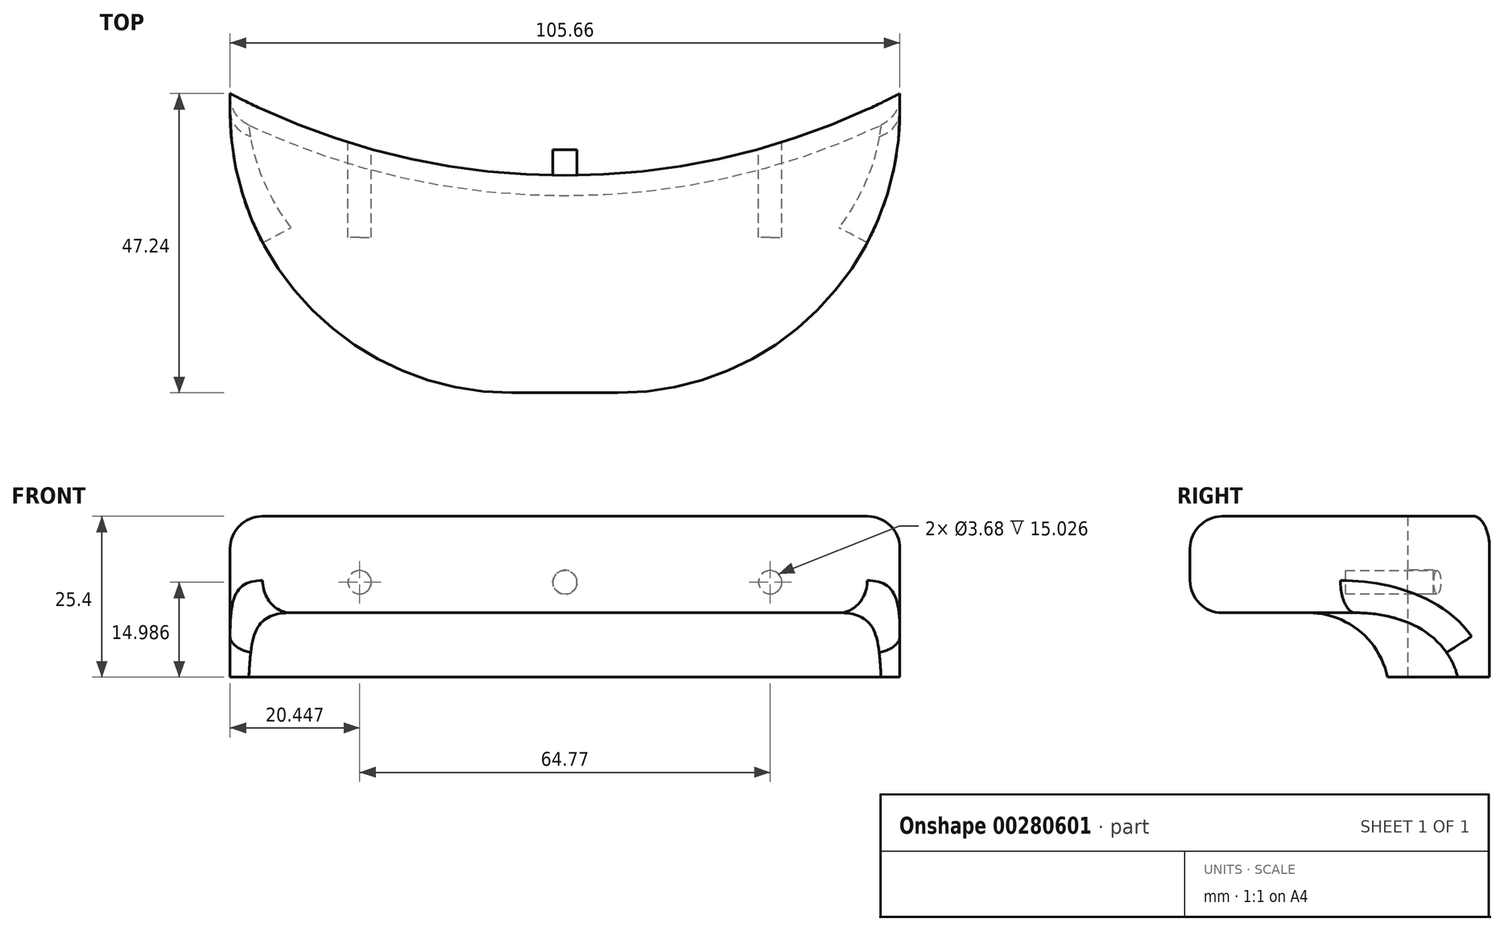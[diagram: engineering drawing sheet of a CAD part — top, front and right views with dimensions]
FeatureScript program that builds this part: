
annotation { "Feature Type Name" : "Feature", "Feature Type Description" : "" }
export const myFeature = defineFeature(function(context is Context, id is Id, definition is map)
    precondition{}
    {
        {
            var Q0;
            Q0=qCreatedBy(makeId("Top.planeOp"),FACE);
            var sketch = newSketch(context, id + "F0", { "sketchPlane" : qUnion([Q0])});
            skLineSegment(sketch, "E0.bottom", {"start": v(44.45, 0) * mm, "end": v(61.21, 0) * mm});
            skLineSegment(sketch, "E0.left", {"start": v(0, 44.45) * mm, "end": v(0, 47.24) * mm});
            skLineSegment(sketch, "E0.right", {"start": v(105.66, 44.45) * mm, "end": v(105.66, 47.24) * mm});
            skArc(sketch, "E1", {"start": v(0, 47.24) * mm, "mid": v(52.83, 34.3) * mm, "end": v(105.66, 47.24) * mm});
            skPoint(sketch, "E2.visualSharp", {"position": v(0, 0) * mm});
            skArc(sketch, "E2.filletArc", {"start": v(0, 44.45) * mm, "mid": v(13.02, 13.02) * mm, "end": v(44.45, 0) * mm});
            skPoint(sketch, "E3.visualSharp", {"position": v(105.66, 0) * mm});
            skArc(sketch, "E3.filletArc", {"start": v(61.21, 0) * mm, "mid": v(92.64, 13.02) * mm, "end": v(105.66, 44.45) * mm});
            skSolve(sketch);
        }
        {
            var Q0;
            Q0 = qSketchRegion(id + "F0", true);
            extrude(context, id + "F1", {"entities" : qUnion([Q0]), "depth" : 25.4 * mm});
        }
        {
            var Q0;
            Q0=makeQuery(id+"F1.opExtrude","CAP_FACE",FACE,{"disambiguationData":[OSD([sQuery(id+"F0.wireOp",EDGE,"E0.bottom"),sQuery(id+"F0.wireOp",EDGE,"E0.left"),sQuery(id+"F0.wireOp",EDGE,"E0.right"),sQuery(id+"F0.wireOp",EDGE,"E1"),sQuery(id+"F0.wireOp",EDGE,"E2.filletArc"),sQuery(id+"F0.wireOp",EDGE,"E3.filletArc")])],"isStart":true});
            var sketch = newSketch(context, id + "F2", { "sketchPlane" : qUnion([Q0])});
            skArc(sketch, "E4.0", {"start": v(-1.47, -44.43) * mm, "mid": v(52.83, -31.13) * mm, "end": v(107.13, -44.43) * mm});
            skLineSegment(sketch, "E5", {"start": v(-1.47, -44.43) * mm, "end": v(-1.47, 12.03) * mm});
            skLineSegment(sketch, "E6", {"start": v(107.13, -44.43) * mm, "end": v(107.13, 12.98) * mm});
            skLineSegment(sketch, "E7", {"start": v(107.13, 12.98) * mm, "end": v(-1.47, 12.03) * mm});
            skSolve(sketch);
        }
        {
            var Q0;
            Q0 = qSketchRegion(id + "F2", true);
            extrude(context, id + "F3", {"entities" : qUnion([Q0]), "operationType" : NewBodyOperationType.REMOVE, "oppositeDirection" : true, "depth" : 10.16 * mm});
        }
        {
            var Q0;
            Q0=makeQuery(id+"F3.boolean.opBoolean","COPY",EDGE,{"derivedFrom":makeQuery(id+"F3.opExtrude","CAP_EDGE",EDGE,{"disambiguationData":[OSD([sQuery(id+"F2.wireOp",EDGE,"E4.0")])],"isStart":false})});
            fillet(context, id + "F4", {"entities" : qUnion([Q0]), "radius" : 12.7 * mm, "tangentPropagation" : true, "allowEdgeOverflow" : false});
        }
        {
            var Q0;
            Q0=makeQuery(id+"F1.opExtrude","CAP_EDGE",EDGE,{"disambiguationData":[OSD([sQuery(id+"F0.wireOp",EDGE,"E2.filletArc")])],"isStart":false});
            fillet(context, id + "F5", {"entities" : qUnion([Q0]), "radius" : 5.08 * mm, "tangentPropagation" : true, "allowEdgeOverflow" : false});
        }
        {
            var Q0;
            Q0=makeQuery(id+"F3.boolean.opBoolean","INTERSECT",EDGE,{"derivedFrom":[makeQuery(id+"F1.opExtrude","SWEPT_FACE",FACE,{"disambiguationData":[OSD([sQuery(id+"F0.wireOp",EDGE,"E2.filletArc")])]}),makeQuery(id+"F3.opExtrude","CAP_FACE",FACE,{"disambiguationData":[OSD([sQuery(id+"F2.wireOp",EDGE,"E4.0"),sQuery(id+"F2.wireOp",EDGE,"E5"),sQuery(id+"F2.wireOp",EDGE,"E6"),sQuery(id+"F2.wireOp",EDGE,"E7")])],"isStart":false})]});
            fillet(context, id + "F6", {"entities" : qUnion([Q0]), "radius" : 5.08 * mm, "tangentPropagation" : true, "allowEdgeOverflow" : false});
        }
        {
            var Q0;
            Q0=makeQuery(id+"F1.opExtrude","CAP_EDGE",EDGE,{"disambiguationData":[OSD([sQuery(id+"F0.wireOp",EDGE,"E1")])],"isStart":false});
            cPoint(context, id + "F7", {"entities" : qUnion([Q0]), "parameter" : 0.5});
        }
        {
            var Q0;
            Q0=qCreatedBy(makeId("Front.planeOp"),FACE);
            var Q1;
            Q1 = qCreatedBy(id + "F7" ,VERTEX);
            cPlane(context, id + "F8", {"entities" : qUnion([Q0, Q1]), "cplaneType" : CPlaneType.PLANE_POINT, "offset" : 25.4 * mm, "oppositeDirection" : true, "width" : 152.4 * mm, "height" : 152.4 * mm});
        }
        {
            var Q0;
            Q0=qCreatedBy(id+"F8.planeOp",FACE);
            var sketch = newSketch(context, id + "F9", { "sketchPlane" : qUnion([Q0])});
            skCircle(sketch, "E8", {"center": v(52.83, 14.99) * mm, "radius": 1.9 * mm});
            skSolve(sketch);
        }
        {
            var Q0;
            Q0 = qSketchRegion(id + "F9", true);
            extrude(context, id + "F10", {"entities" : qUnion([Q0]), "operationType" : NewBodyOperationType.ADD, "oppositeDirection" : true, "depth" : 4.06 * mm});
        }
        {
            var Q0;
            Q0=qCreatedBy(id+"F8.planeOp",FACE);
            var sketch = newSketch(context, id + "F11", { "sketchPlane" : qUnion([Q0])});
            skCircle(sketch, "E9", {"center": v(85.22, 14.99) * mm, "radius": 1.84 * mm});
            skCircle(sketch, "E10", {"center": v(20.45, 14.99) * mm, "radius": 1.84 * mm});
            skLineSegment(sketch, "E11", {"start": v(52.83, 30.07) * mm, "end": v(52.83, -19.42) * mm, "construction": true});
            skSolve(sketch);
        }
        {
            var Q0;
            Q0 = qSketchRegion(id + "F11", true);
            extrude(context, id + "F12", {"entities" : qUnion([Q0]), "operationType" : NewBodyOperationType.REMOVE, "endBound" : BoundingType.SYMMETRIC, "depth" : 19.56 * mm});
        }
    });
